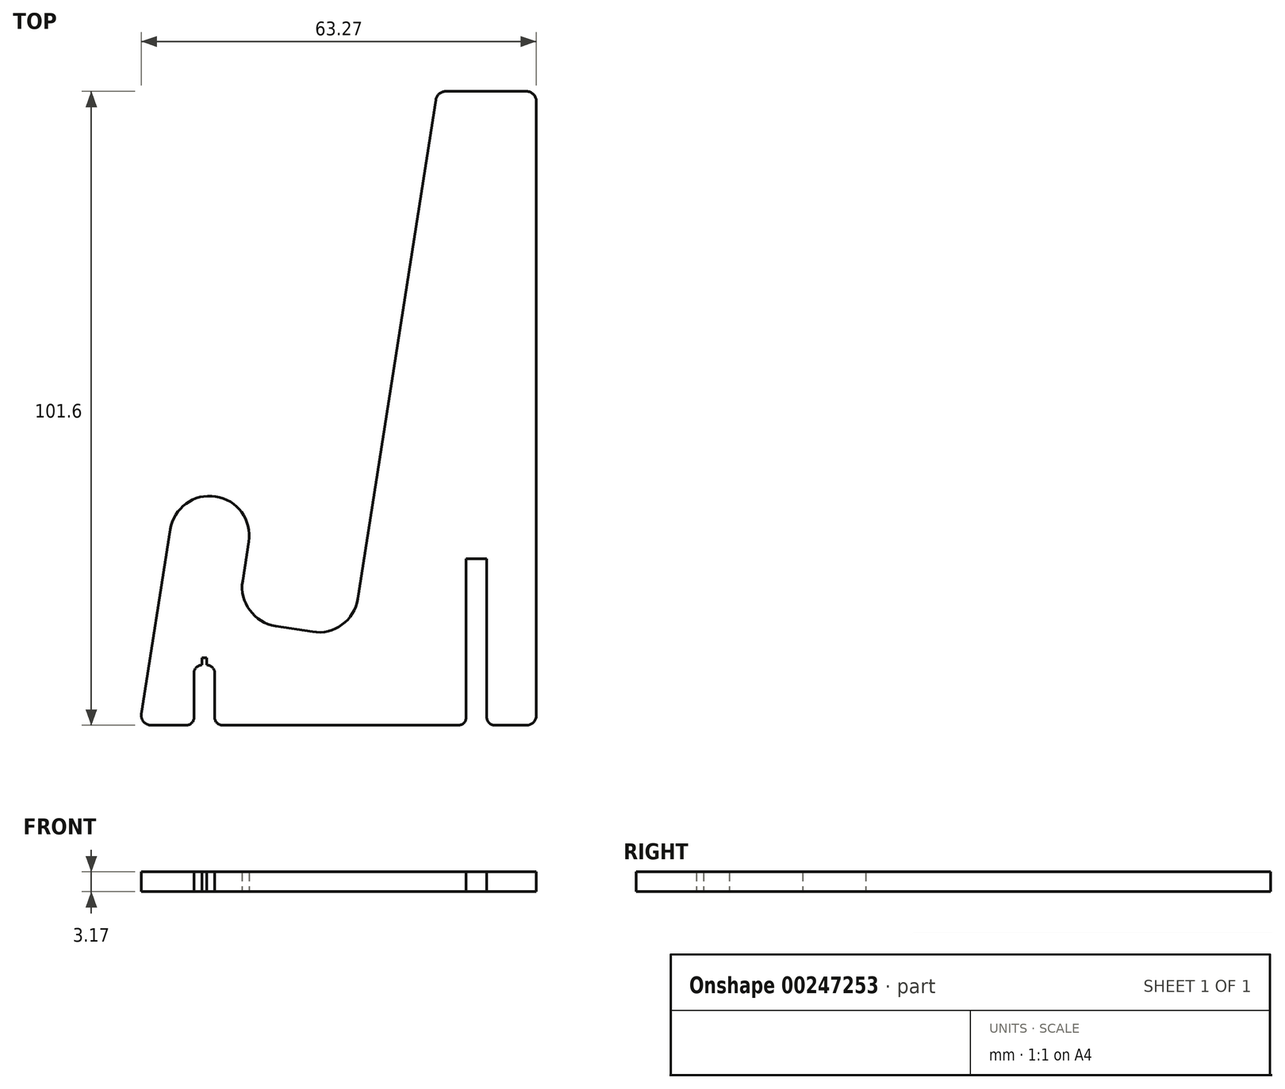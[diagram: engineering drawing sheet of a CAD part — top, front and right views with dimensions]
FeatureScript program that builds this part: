
annotation { "Feature Type Name" : "Feature", "Feature Type Description" : "" }
export const myFeature = defineFeature(function(context is Context, id is Id, definition is map)
    precondition{}
    {
        {
            var Q0;
            Q0=qCreatedBy(makeId("Top.planeOp"),FACE);
            var sketch = newSketch(context, id + "F0", { "sketchPlane" : qUnion([Q0])});
            skLineSegment(sketch, "E0.top", {"start": v(30.18, -50.8) * mm, "end": v(23.83, -50.8) * mm});
            skLineSegment(sketch, "E0.left", {"start": v(31.77, 49.21) * mm, "end": v(31.77, -49.21) * mm});
            skPoint(sketch, "E0.middle", {"position": v(0, 0) * mm});
            skLineSegment(sketch, "E1", {"start": v(15.67, 49.46) * mm, "end": v(2.19, -36.8) * mm});
            skLineSegment(sketch, "E2", {"start": v(3.17, -30.52) * mm, "end": v(15.67, 49.46) * mm});
            skPoint(sketch, "E3.orphan", {"position": v(0, 50.8) * mm});
            skLineSegment(sketch, "E4", {"start": v(30.18, 50.8) * mm, "end": v(17.24, 50.8) * mm});
            skLineSegment(sketch, "E5", {"start": v(-29.91, -50.8) * mm, "end": v(-23.05, -50.8) * mm});
            skLineSegment(sketch, "E6", {"start": v(-26.86, -19.43) * mm, "end": v(-31.48, -48.97) * mm});
            skLineSegment(sketch, "E7", {"start": v(-31.48, -48.97) * mm, "end": v(-26.86, -19.43) * mm});
            skLineSegment(sketch, "E8", {"start": v(-14.3, -21.37) * mm, "end": v(-15.28, -27.64) * mm});
            skLineSegment(sketch, "E9", {"start": v(-16.26, -33.91) * mm, "end": v(2.19, -36.8) * mm});
            skLineSegment(sketch, "E10", {"start": v(-4.08, -35.82) * mm, "end": v(-9.98, -34.9) * mm});
            skArc(sketch, "E11", {"start": v(-14.3, -21.37) * mm, "mid": v(-19.61, -14.11) * mm, "end": v(-26.86, -19.43) * mm});
            skPoint(sketch, "E0.right.start.orphan", {"position": v(-31.77, 50.8) * mm});
            skPoint(sketch, "E12.visualSharp", {"position": v(-16.26, -33.91) * mm});
            skArc(sketch, "E12.filletArc", {"start": v(-15.28, -27.64) * mm, "mid": v(-14.13, -32.36) * mm, "end": v(-9.98, -34.9) * mm});
            skPoint(sketch, "E13.visualSharp", {"position": v(2.19, -36.8) * mm});
            skArc(sketch, "E13.filletArc", {"start": v(-4.08, -35.82) * mm, "mid": v(0.64, -34.67) * mm, "end": v(3.17, -30.52) * mm});
            skPoint(sketch, "E14.visualSharp", {"position": v(15.88, 50.8) * mm});
            skArc(sketch, "E14.filletArc", {"start": v(17.24, 50.8) * mm, "mid": v(16.2, 50.42) * mm, "end": v(15.67, 49.46) * mm});
            skPoint(sketch, "E15.visualSharp", {"position": v(31.77, 50.8) * mm});
            skArc(sketch, "E15.filletArc", {"start": v(31.77, 49.21) * mm, "mid": v(31.3, 50.34) * mm, "end": v(30.18, 50.8) * mm});
            skPoint(sketch, "E16.visualSharp", {"position": v(31.77, -50.8) * mm});
            skArc(sketch, "E16.filletArc", {"start": v(30.18, -50.8) * mm, "mid": v(31.3, -50.34) * mm, "end": v(31.77, -49.21) * mm});
            skPoint(sketch, "E17.visualSharp", {"position": v(-31.77, -50.8) * mm});
            skArc(sketch, "E17.filletArc", {"start": v(-31.48, -48.97) * mm, "mid": v(-31.12, -50.24) * mm, "end": v(-29.91, -50.8) * mm});
            skLineSegment(sketch, "E18.left", {"start": v(-23.05, -50.8) * mm, "end": v(-23.05, -41.15) * mm});
            skLineSegment(sketch, "E18.right", {"start": v(-19.75, -50.8) * mm, "end": v(-19.75, -41.15) * mm});
            skLineSegment(sketch, "E19.trimOffspring", {"start": v(-19.75, -50.8) * mm, "end": v(0, -50.8) * mm});
            skLineSegment(sketch, "E20", {"start": v(-23.05, -41.15) * mm, "end": v(-19.75, -41.15) * mm});
            skLineSegment(sketch, "E21.left", {"start": v(20.53, -50.8) * mm, "end": v(20.53, -24.13) * mm});
            skLineSegment(sketch, "E21.right", {"start": v(23.83, -50.8) * mm, "end": v(23.83, -24.13) * mm});
            skLineSegment(sketch, "E22", {"start": v(20.53, -24.13) * mm, "end": v(23.83, -24.13) * mm});
            skPoint(sketch, "E22.endSnap0", {"position": v(23.83, -25.4) * mm});
            skPoint(sketch, "E21.top.end.orphan", {"position": v(23.83, 0) * mm});
            skLineSegment(sketch, "E23.trimOffspring", {"start": v(-23.05, -50.8) * mm, "end": v(-29.91, -50.8) * mm});
            skLineSegment(sketch, "E24.trimOffspring", {"start": v(20.53, -50.8) * mm, "end": v(-19.75, -50.8) * mm});
            skSolve(sketch);
        }
        {
            var Q0;
            Q0 = qSketchRegion(id + "F0", true);
            extrude(context, id + "F1", {"entities" : qUnion([Q0]), "depth" : 3.17 * mm});
        }
        {
            var Q0;
            Q0=makeQuery(id+"F1.opExtrude","SWEPT_EDGE",EDGE,{"disambiguationData":[OSD([sQuery(id+"F0.wireOp",EDGE,"E0.top"),sQuery(id+"F0.wireOp",EDGE,"E21.right")])]});
            var Q1;
            Q1=makeQuery(id+"F1.opExtrude","SWEPT_EDGE",EDGE,{"disambiguationData":[OSD([sQuery(id+"F0.wireOp",EDGE,"E18.right"),sQuery(id+"F0.wireOp",EDGE,"E24.trimOffspring")])]});
            var Q2;
            Q2=makeQuery(id+"F1.opExtrude","SWEPT_EDGE",EDGE,{"disambiguationData":[OSD([sQuery(id+"F0.wireOp",EDGE,"E21.left"),sQuery(id+"F0.wireOp",EDGE,"E24.trimOffspring")])]});
            var Q3;
            Q3=makeQuery(id+"F1.opExtrude","SWEPT_EDGE",EDGE,{"disambiguationData":[OSD([sQuery(id+"F0.wireOp",EDGE,"E18.left"),sQuery(id+"F0.wireOp",EDGE,"E23.trimOffspring")])]});
            fillet(context, id + "F2", {"entities" : qUnion([Q0, Q1, Q2, Q3]), "radius" : 1.27 * mm, "tangentPropagation" : true, "allowEdgeOverflow" : false});
        }
        {
            var Q0;
            Q0=makeQuery(id+"F1.opExtrude","SWEPT_FACE",FACE,{"disambiguationData":[OSD([sQuery(id+"F0.wireOp",EDGE,"E20")])]});
            extrude(context, id + "F3", {"entities" : qUnion([Q0]), "operationType" : NewBodyOperationType.REMOVE, "oppositeDirection" : true, "depth" : 1.14 * mm});
        }
    });
